# Revit family: MT-HB_SLIDING DOOR_XXXXX
name_source: partatom
category: Doors
revit_build: Autodesk Revit 2017 (Build: 20160225_1515(x64)
units: mm (PartAtom-declared; Revit-internal decimal feet)

## family parameters
Always vertical = Yes
Cut with Voids When Loaded = No
Host = Wall
OmniClass Number = 23.30.20.00
OmniClass Title = Windows
Room Calculation Point = No
Shared = No

## types (2) — shared parameters
ANZRC COMPLIANT = YES
Analytic Construction = <None>
BOT PANEL POSITION = 35 mm  [stored 0.114829 ft]
DOUBLE GLAZED THICKNESS = 18 mm  [stored 0.0590551 ft]
FRAME MATERIAL = <By Category>
GLAZED MATERIAL = Glass
MAX HEIGHT = 3000 mm  [stored 9.84252 ft]
MAX PANEL HEIGHT = 3000 mm  [stored 9.84252 ft]
MAX PANEL WIDTH = 1250 mm  [stored 4.10105 ft]
MAX WIDTH = 5000 mm  [stored 16.4042 ft]
Manufacturer = ALSPEC
Model = HAWKESBURY TOP HUNG COMMERCIAL SLIDING DOOR
OFFSET = 10 mm  [stored 0.0328084 ft]
SINGLE GLAZED THICKNESS = 5 mm  [stored 0.0164042 ft]
URL = WWW.ALSPEC.COM.AU
VERSION = 2.1
WARNING = No
Wall Closure = By host
YEAR = 2019
zero-valued in all types: Default Sill Height, TOLERANCE

## per-type parameters (varying)
| type | 1L1R | 2L/2R | A | AIR POCKET | DOUBLE GLAZED | Height | OVERALL FRAME HEIGHT | OVERALL FRAME WIDTH | PANEL HEIGHT | PANEL WIDTH | Rough Height | Rough Width | TOP PANEL POSITION | Width |
| XXXXX | No | Yes | 75 mm | 8 mm  [stored 0.0262467 ft] | No | 3000 mm  [stored 9.84252 ft] | 3000 mm  [stored 9.84252 ft] | 5000 mm  [stored 16.4042 ft] | 2890 mm  [stored 9.48163 ft] | 1045 mm | 3000 mm  [stored 9.84252 ft] | 5000 mm  [stored 16.4042 ft] | 2874 mm  [stored 9.42913 ft] | 5500 mm  [stored 18.0446 ft] |
| 1L1R | Yes | No | 169 mm | 5 mm  [stored 0.0164042 ft] | Yes | 2100 mm | 2100 mm | 2000 mm  [stored 6.56168 ft] | 1990 mm | 445 mm | 2100 mm | 2000 mm  [stored 6.56168 ft] | 1974 mm | 2000 mm  [stored 6.56168 ft] |

note: [stored X ft] marks values corroborated as IEEE doubles in the binary element streams (Revit-internal decimal feet)

## geometry (parser evidence)
native form markers: Extrusion x1, Sweep x50
no freeform markers — native parametric forms only
